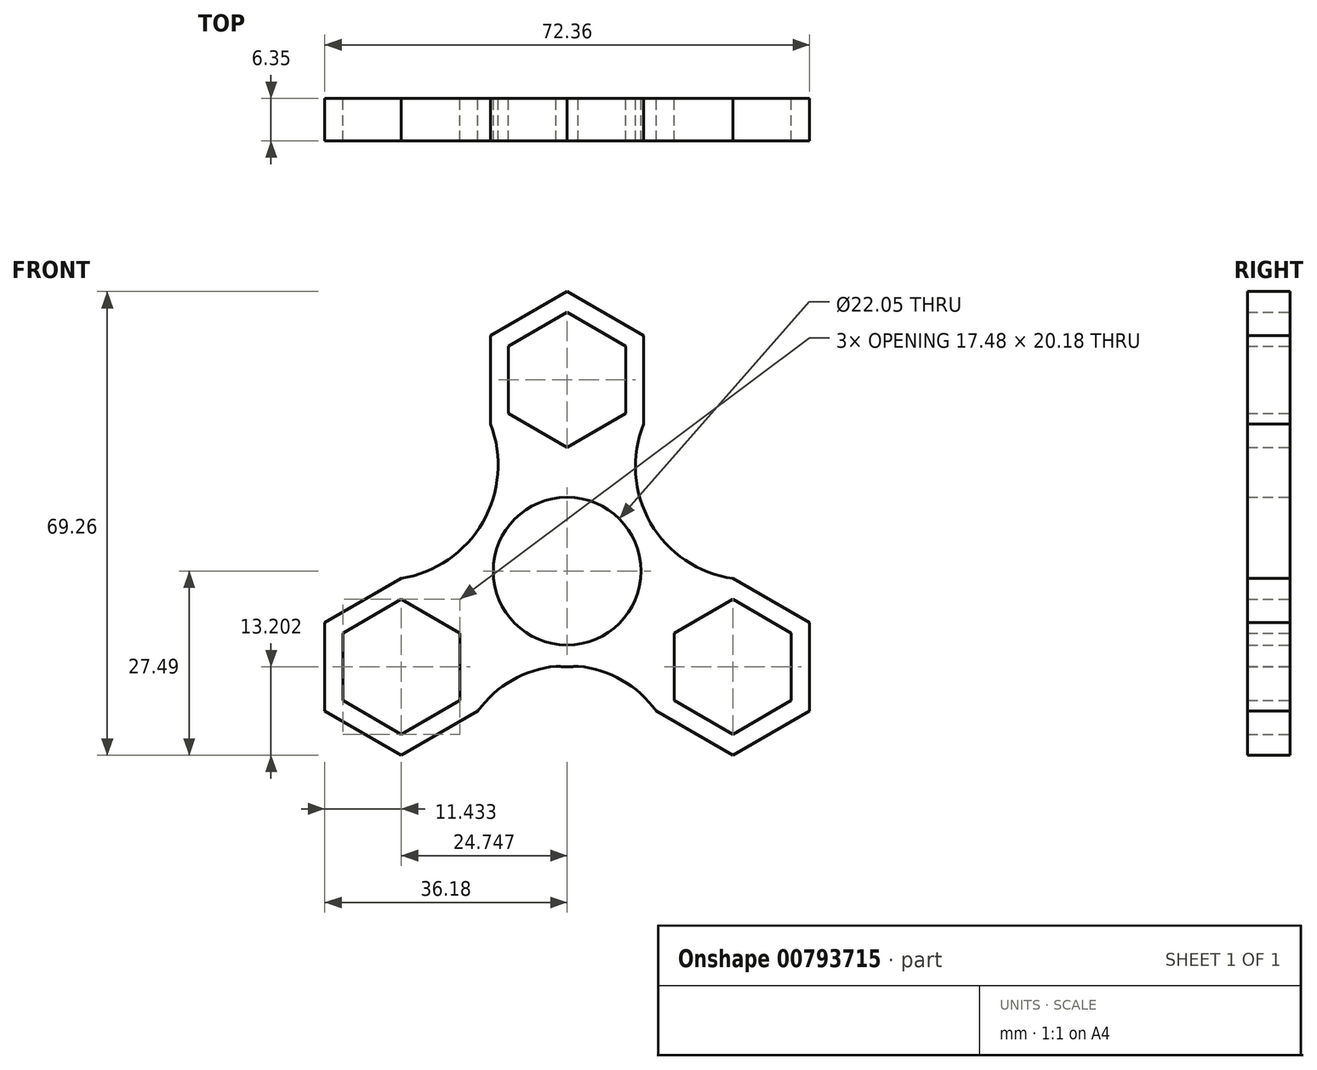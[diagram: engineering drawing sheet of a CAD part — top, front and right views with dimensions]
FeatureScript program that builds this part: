
annotation { "Feature Type Name" : "Feature", "Feature Type Description" : "" }
export const myFeature = defineFeature(function(context is Context, id is Id, definition is map)
    precondition{}
    {
        {
            var Q0;
            Q0=qCreatedBy(makeId("Front.planeOp"),FACE);
            var sketch = newSketch(context, id + "F0", { "sketchPlane" : qUnion([Q0])});
            skCircle(sketch, "E0", {"center": v(0, 0) * mm, "radius": 11.02 * mm});
            skCircle(sketch, "E1", {"center": v(0, 0) * mm, "radius": 14.29 * mm});
            skCircle(sketch, "E2.cCircle", {"center": v(0, 28.58) * mm, "radius": 8.74 * mm, "construction": true});
            skLineSegment(sketch, "E2.0", {"start": v(8.74, 33.62) * mm, "end": v(8.74, 23.53) * mm});
            skLineSegment(sketch, "E2.1", {"start": v(8.74, 23.53) * mm, "end": v(0, 18.49) * mm});
            skLineSegment(sketch, "E2.2", {"start": v(0, 18.49) * mm, "end": v(-8.74, 23.53) * mm});
            skLineSegment(sketch, "E2.3", {"start": v(-8.74, 23.53) * mm, "end": v(-8.74, 33.62) * mm});
            skLineSegment(sketch, "E2.4", {"start": v(-8.74, 33.62) * mm, "end": v(0, 38.66) * mm});
            skLineSegment(sketch, "E2.5", {"start": v(0, 38.66) * mm, "end": v(8.74, 33.62) * mm});
            skPoint(sketch, "E2.0.midPoint", {"position": v(8.74, 28.58) * mm});
            skCircle(sketch, "E3.cCircle", {"center": v(0, 28.58) * mm, "radius": 11.43 * mm, "construction": true});
            skLineSegment(sketch, "E3.0", {"start": v(-11.43, 21.98) * mm, "end": v(-11.43, 35.17) * mm});
            skLineSegment(sketch, "E3.1", {"start": v(-11.43, 35.17) * mm, "end": v(0, 41.77) * mm});
            skLineSegment(sketch, "E3.2", {"start": v(0, 41.77) * mm, "end": v(11.43, 35.17) * mm});
            skLineSegment(sketch, "E3.3", {"start": v(11.43, 35.17) * mm, "end": v(11.43, 21.98) * mm});
            skLineSegment(sketch, "E3.4", {"start": v(11.43, 21.98) * mm, "end": v(0, 15.38) * mm});
            skLineSegment(sketch, "E3.5", {"start": v(0, 15.38) * mm, "end": v(-11.43, 21.98) * mm});
            skPoint(sketch, "E3.0.midPoint", {"position": v(-11.43, 28.58) * mm});
            skLineSegment(sketch, "E4.1.0", {"start": v(-33.48, -9.24) * mm, "end": v(-24.75, -4.2) * mm});
            skPoint(sketch, "E4.1.1", {"position": v(-19.03, -24.19) * mm});
            skCircle(sketch, "E4.1.2", {"center": v(-24.75, -14.29) * mm, "radius": 8.74 * mm, "construction": true});
            skLineSegment(sketch, "E4.1.5", {"start": v(-16, -9.24) * mm, "end": v(-16, -19.33) * mm});
            skLineSegment(sketch, "E4.1.6", {"start": v(-13.32, -7.69) * mm, "end": v(-13.32, -20.89) * mm});
            skLineSegment(sketch, "E4.1.7", {"start": v(-24.75, -1.09) * mm, "end": v(-13.32, -7.69) * mm});
            skLineSegment(sketch, "E4.1.8", {"start": v(-36.18, -7.69) * mm, "end": v(-24.75, -1.09) * mm});
            skLineSegment(sketch, "E4.1.9", {"start": v(-24.75, -4.2) * mm, "end": v(-16, -9.24) * mm});
            skLineSegment(sketch, "E4.1.10", {"start": v(-24.75, -24.38) * mm, "end": v(-33.48, -19.33) * mm});
            skLineSegment(sketch, "E4.1.11", {"start": v(-33.48, -19.33) * mm, "end": v(-33.48, -9.24) * mm});
            skCircle(sketch, "E4.1.12", {"center": v(-24.75, -14.29) * mm, "radius": 11.43 * mm, "construction": true});
            skLineSegment(sketch, "E4.1.13", {"start": v(-13.32, -20.89) * mm, "end": v(-24.75, -27.49) * mm});
            skLineSegment(sketch, "E4.1.14", {"start": v(-24.75, -27.49) * mm, "end": v(-36.18, -20.89) * mm});
            skLineSegment(sketch, "E4.1.15", {"start": v(-36.18, -20.89) * mm, "end": v(-36.18, -7.69) * mm});
            skPoint(sketch, "E4.1.16", {"position": v(-29.12, -6.72) * mm});
            skLineSegment(sketch, "E4.1.17", {"start": v(-16, -19.33) * mm, "end": v(-24.75, -24.38) * mm});
            skLineSegment(sketch, "E4.2.0", {"start": v(24.75, -24.38) * mm, "end": v(16, -19.33) * mm});
            skPoint(sketch, "E4.2.1", {"position": v(30.46, -4.39) * mm});
            skCircle(sketch, "E4.2.2", {"center": v(24.75, -14.29) * mm, "radius": 8.74 * mm, "construction": true});
            skLineSegment(sketch, "E4.2.5", {"start": v(16, -9.24) * mm, "end": v(24.75, -4.2) * mm});
            skLineSegment(sketch, "E4.2.6", {"start": v(13.32, -7.69) * mm, "end": v(24.75, -1.09) * mm});
            skLineSegment(sketch, "E4.2.7", {"start": v(13.32, -20.89) * mm, "end": v(13.32, -7.69) * mm});
            skLineSegment(sketch, "E4.2.8", {"start": v(24.75, -27.49) * mm, "end": v(13.32, -20.89) * mm});
            skLineSegment(sketch, "E4.2.9", {"start": v(16, -19.33) * mm, "end": v(16, -9.24) * mm});
            skLineSegment(sketch, "E4.2.10", {"start": v(33.48, -9.24) * mm, "end": v(33.48, -19.33) * mm});
            skLineSegment(sketch, "E4.2.11", {"start": v(33.48, -19.33) * mm, "end": v(24.75, -24.38) * mm});
            skCircle(sketch, "E4.2.12", {"center": v(24.75, -14.29) * mm, "radius": 11.43 * mm, "construction": true});
            skLineSegment(sketch, "E4.2.13", {"start": v(24.75, -1.09) * mm, "end": v(36.18, -7.69) * mm});
            skLineSegment(sketch, "E4.2.14", {"start": v(36.18, -7.69) * mm, "end": v(36.18, -20.89) * mm});
            skLineSegment(sketch, "E4.2.15", {"start": v(36.18, -20.89) * mm, "end": v(24.75, -27.49) * mm});
            skPoint(sketch, "E4.2.16", {"position": v(20.38, -21.85) * mm});
            skLineSegment(sketch, "E4.2.17", {"start": v(24.75, -4.2) * mm, "end": v(33.48, -9.24) * mm});
            skArc(sketch, "E5", {"start": v(-24.75, -1.09) * mm, "mid": v(-12.61, 7.28) * mm, "end": v(-11.43, 21.98) * mm});
            skArc(sketch, "E6", {"start": v(11.43, 21.98) * mm, "mid": v(12.46, 7.2) * mm, "end": v(24.75, -1.09) * mm});
            skArc(sketch, "E7", {"start": v(13.32, -20.89) * mm, "mid": v(0, -14.11) * mm, "end": v(-13.32, -20.89) * mm});
            skSolve(sketch);
        }
        {
            var Q0;
            Q0 = qSketchRegion(id + "F0", true);
            extrude(context, id + "F1", {"entities" : qUnion([Q0]), "depth" : 6.35 * mm, "offsetDistance" : 25.4 * mm});
        }
    });
